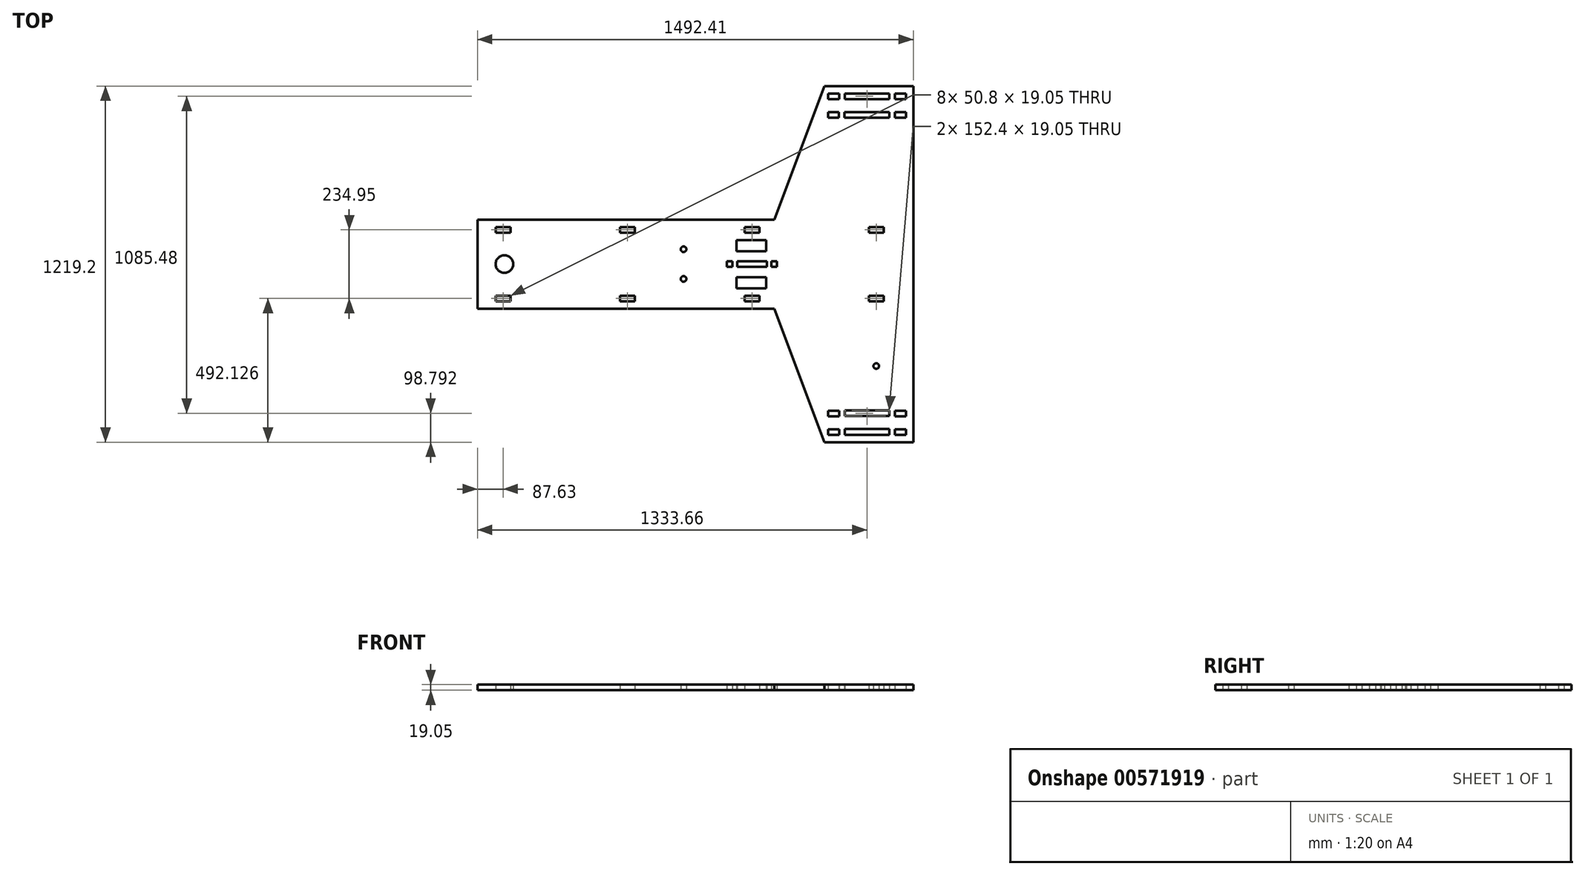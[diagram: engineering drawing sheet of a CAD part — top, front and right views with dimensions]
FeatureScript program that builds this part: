
annotation { "Feature Type Name" : "Feature", "Feature Type Description" : "" }
export const myFeature = defineFeature(function(context is Context, id is Id, definition is map)
    precondition{}
    {
        {
            var Q0;
            Q0=qCreatedBy(makeId("Top.planeOp"),FACE);
            var sketch = newSketch(context, id + "F0", { "sketchPlane" : qUnion([Q0])});
            skLineSegment(sketch, "E0.left", {"start": v(578, -643.36) * mm, "end": v(578, 575.84) * mm});
            skLineSegment(sketch, "E1.bottom", {"start": v(-914.4, 93.24) * mm, "end": v(101.6, 93.24) * mm});
            skLineSegment(sketch, "E1.top", {"start": v(-914.4, -186.16) * mm, "end": v(101.6, -186.16) * mm});
            skLineSegment(sketch, "E1.left", {"start": v(-914.4, 93.24) * mm, "end": v(-914.4, -186.16) * mm});
            skLineSegment(sketch, "E1.right", {"start": v(101.6, 93.24) * mm, "end": v(101.6, -186.16) * mm});
            skPoint(sketch, "E2.oppositeSnap0", {"position": v(-603.2, 271.04) * mm});
            skPoint(sketch, "E3.centerSnap0", {"position": v(-914.4, -46.46) * mm});
            skLineSegment(sketch, "E4.left", {"start": v(-914.4, -186.16) * mm, "end": v(-914.4, -167.1) * mm});
            skLineSegment(sketch, "E4.right", {"start": v(578, -186.16) * mm, "end": v(578, -167.1) * mm});
            skLineSegment(sketch, "E5.left", {"start": v(-914.4, 93.24) * mm, "end": v(-914.4, 74.2) * mm});
            skLineSegment(sketch, "E5.right", {"start": v(578, 93.24) * mm, "end": v(578, 74.2) * mm});
            skLineSegment(sketch, "E6", {"start": v(578, -643.36) * mm, "end": v(273.2, -643.36) * mm});
            skLineSegment(sketch, "E7", {"start": v(273.2, -643.36) * mm, "end": v(101.6, -186.16) * mm});
            skLineSegment(sketch, "E8", {"start": v(578, 575.84) * mm, "end": v(273.2, 575.84) * mm});
            skLineSegment(sketch, "E9.bottom", {"start": v(-852.17, -141.7) * mm, "end": v(-801.37, -141.7) * mm});
            skLineSegment(sketch, "E9.top", {"start": v(-852.17, -160.76) * mm, "end": v(-801.37, -160.76) * mm});
            skLineSegment(sketch, "E9.left", {"start": v(-852.17, -141.7) * mm, "end": v(-852.17, -160.76) * mm});
            skLineSegment(sketch, "E9.right", {"start": v(-801.37, -141.7) * mm, "end": v(-801.37, -160.76) * mm});
            skLineSegment(sketch, "E10", {"start": v(-852.17, -160.76) * mm, "end": v(101.6, -160.76) * mm});
            skLineSegment(sketch, "E11.bottom", {"start": v(-375.29, -160.76) * mm, "end": v(-426.09, -160.76) * mm});
            skLineSegment(sketch, "E11.top", {"start": v(-375.29, -141.7) * mm, "end": v(-426.09, -141.7) * mm});
            skLineSegment(sketch, "E11.left", {"start": v(-375.29, -160.76) * mm, "end": v(-375.29, -141.7) * mm});
            skLineSegment(sketch, "E11.right", {"start": v(-426.09, -160.76) * mm, "end": v(-426.09, -141.7) * mm});
            skLineSegment(sketch, "E12.bottom", {"start": v(0, -160.76) * mm, "end": v(50.8, -160.76) * mm});
            skLineSegment(sketch, "E12.top", {"start": v(0, -141.7) * mm, "end": v(50.8, -141.7) * mm});
            skLineSegment(sketch, "E12.left", {"start": v(0, -160.76) * mm, "end": v(0, -141.7) * mm});
            skLineSegment(sketch, "E12.right", {"start": v(50.8, -160.76) * mm, "end": v(50.8, -141.7) * mm});
            skLineSegment(sketch, "E13", {"start": v(101.6, -160.76) * mm, "end": v(578, -160.76) * mm});
            skLineSegment(sketch, "E14", {"start": v(101.6, 93.24) * mm, "end": v(578, 93.24) * mm});
            skLineSegment(sketch, "E15.bottom", {"start": v(426.09, -160.76) * mm, "end": v(476.89, -160.76) * mm});
            skLineSegment(sketch, "E15.top", {"start": v(426.09, -141.7) * mm, "end": v(476.89, -141.7) * mm});
            skLineSegment(sketch, "E15.left", {"start": v(426.09, -160.76) * mm, "end": v(426.09, -141.7) * mm});
            skLineSegment(sketch, "E15.right", {"start": v(476.89, -160.76) * mm, "end": v(476.89, -141.7) * mm});
            skLineSegment(sketch, "E16.bottom", {"start": v(101.6, 93.24) * mm, "end": v(-914.4, 93.24) * mm});
            skLineSegment(sketch, "E16.top", {"start": v(101.6, 118.64) * mm, "end": v(-914.4, 118.64) * mm});
            skLineSegment(sketch, "E16.left", {"start": v(101.6, 93.24) * mm, "end": v(101.6, 118.64) * mm});
            skLineSegment(sketch, "E16.right", {"start": v(-914.4, 93.24) * mm, "end": v(-914.4, 118.64) * mm});
            skLineSegment(sketch, "E17", {"start": v(101.6, 118.64) * mm, "end": v(273.2, 575.84) * mm});
            skLineSegment(sketch, "E18.bottom", {"start": v(-852.17, 93.24) * mm, "end": v(-801.37, 93.24) * mm});
            skLineSegment(sketch, "E18.top", {"start": v(-852.17, 74.2) * mm, "end": v(-801.37, 74.2) * mm});
            skLineSegment(sketch, "E18.left", {"start": v(-852.17, 93.24) * mm, "end": v(-852.17, 74.2) * mm});
            skLineSegment(sketch, "E18.right", {"start": v(-801.37, 93.24) * mm, "end": v(-801.37, 74.2) * mm});
            skLineSegment(sketch, "E19", {"start": v(-801.37, 93.24) * mm, "end": v(-426.08, 93.24) * mm});
            skLineSegment(sketch, "E20.bottom", {"start": v(-426.08, 93.24) * mm, "end": v(-375.28, 93.24) * mm});
            skLineSegment(sketch, "E20.top", {"start": v(-426.08, 74.2) * mm, "end": v(-375.28, 74.2) * mm});
            skLineSegment(sketch, "E20.left", {"start": v(-426.08, 93.24) * mm, "end": v(-426.08, 74.2) * mm});
            skLineSegment(sketch, "E20.right", {"start": v(-375.28, 93.24) * mm, "end": v(-375.28, 74.2) * mm});
            skLineSegment(sketch, "E21", {"start": v(-375.28, 93.24) * mm, "end": v(0, 93.24) * mm});
            skLineSegment(sketch, "E22.bottom", {"start": v(0, 93.24) * mm, "end": v(50.8, 93.24) * mm});
            skLineSegment(sketch, "E22.top", {"start": v(0, 74.2) * mm, "end": v(50.8, 74.2) * mm});
            skLineSegment(sketch, "E22.left", {"start": v(0, 93.24) * mm, "end": v(0, 74.2) * mm});
            skLineSegment(sketch, "E22.right", {"start": v(50.8, 93.24) * mm, "end": v(50.8, 74.2) * mm});
            skLineSegment(sketch, "E23", {"start": v(50.8, 93.24) * mm, "end": v(426.09, 93.24) * mm});
            skLineSegment(sketch, "E24.bottom", {"start": v(426.09, 93.24) * mm, "end": v(476.89, 93.24) * mm});
            skLineSegment(sketch, "E24.top", {"start": v(426.09, 74.2) * mm, "end": v(476.89, 74.2) * mm});
            skLineSegment(sketch, "E24.left", {"start": v(426.09, 93.24) * mm, "end": v(426.09, 74.2) * mm});
            skLineSegment(sketch, "E24.right", {"start": v(476.89, 93.24) * mm, "end": v(476.89, 74.2) * mm});
            skCircle(sketch, "E25", {"center": v(-822.05, -33.76) * mm, "radius": 30.12 * mm});
            skCircle(sketch, "E26", {"center": v(-208.68, 17.04) * mm, "radius": 9.53 * mm});
            skCircle(sketch, "E27", {"center": v(-208.68, -84.56) * mm, "radius": 9.53 * mm});
            skLineSegment(sketch, "E28.bottom", {"start": v(285.9, -598.9) * mm, "end": v(324, -598.9) * mm});
            skLineSegment(sketch, "E28.top", {"start": v(285.9, -617.96) * mm, "end": v(324, -617.96) * mm});
            skLineSegment(sketch, "E28.left", {"start": v(285.9, -598.9) * mm, "end": v(285.9, -617.96) * mm});
            skLineSegment(sketch, "E28.right", {"start": v(324, -598.9) * mm, "end": v(324, -617.96) * mm});
            skLineSegment(sketch, "E29.bottom", {"start": v(514.5, -617.96) * mm, "end": v(552.6, -617.96) * mm});
            skLineSegment(sketch, "E29.top", {"start": v(514.5, -598.9) * mm, "end": v(552.6, -598.9) * mm});
            skLineSegment(sketch, "E29.left", {"start": v(514.5, -617.96) * mm, "end": v(514.5, -598.9) * mm});
            skLineSegment(sketch, "E29.right", {"start": v(552.6, -617.96) * mm, "end": v(552.6, -598.9) * mm});
            skLineSegment(sketch, "E30.bottom", {"start": v(495.46, -598.54) * mm, "end": v(343.06, -598.54) * mm});
            skLineSegment(sketch, "E30.top", {"start": v(495.46, -617.96) * mm, "end": v(343.06, -617.96) * mm});
            skLineSegment(sketch, "E30.left", {"start": v(495.46, -598.54) * mm, "end": v(495.46, -617.96) * mm});
            skLineSegment(sketch, "E30.right", {"start": v(343.06, -598.54) * mm, "end": v(343.06, -617.96) * mm});
            skLineSegment(sketch, "E31.bottom", {"start": v(285.9, 550.44) * mm, "end": v(324, 550.44) * mm});
            skLineSegment(sketch, "E31.top", {"start": v(285.9, 531.4) * mm, "end": v(324, 531.4) * mm});
            skLineSegment(sketch, "E31.left", {"start": v(285.9, 550.44) * mm, "end": v(285.9, 531.4) * mm});
            skLineSegment(sketch, "E31.right", {"start": v(324, 550.44) * mm, "end": v(324, 531.4) * mm});
            skLineSegment(sketch, "E32.bottom", {"start": v(343.06, 550.44) * mm, "end": v(495.46, 550.44) * mm});
            skLineSegment(sketch, "E32.top", {"start": v(343.06, 531.4) * mm, "end": v(495.46, 531.4) * mm});
            skLineSegment(sketch, "E32.left", {"start": v(343.06, 550.44) * mm, "end": v(343.06, 531.4) * mm});
            skLineSegment(sketch, "E32.right", {"start": v(495.46, 550.44) * mm, "end": v(495.46, 531.4) * mm});
            skLineSegment(sketch, "E33.bottom", {"start": v(514.5, 550.44) * mm, "end": v(552.6, 550.44) * mm});
            skLineSegment(sketch, "E33.top", {"start": v(514.5, 531.4) * mm, "end": v(552.6, 531.4) * mm});
            skLineSegment(sketch, "E33.left", {"start": v(514.5, 550.44) * mm, "end": v(514.5, 531.4) * mm});
            skLineSegment(sketch, "E33.right", {"start": v(552.6, 550.44) * mm, "end": v(552.6, 531.4) * mm});
            skLineSegment(sketch, "E34.bottom", {"start": v(514.5, 486.94) * mm, "end": v(552.6, 486.94) * mm});
            skLineSegment(sketch, "E34.top", {"start": v(514.5, 467.9) * mm, "end": v(552.6, 467.9) * mm});
            skLineSegment(sketch, "E34.left", {"start": v(514.5, 486.94) * mm, "end": v(514.5, 467.9) * mm});
            skLineSegment(sketch, "E34.right", {"start": v(552.6, 486.94) * mm, "end": v(552.6, 467.9) * mm});
            skLineSegment(sketch, "E35.bottom", {"start": v(495.46, 486.94) * mm, "end": v(342.54, 486.94) * mm});
            skLineSegment(sketch, "E35.top", {"start": v(495.46, 468) * mm, "end": v(342.54, 468) * mm});
            skLineSegment(sketch, "E35.left", {"start": v(495.46, 486.94) * mm, "end": v(495.46, 468) * mm});
            skLineSegment(sketch, "E35.right", {"start": v(342.54, 486.94) * mm, "end": v(342.54, 468) * mm});
            skLineSegment(sketch, "E36.bottom", {"start": v(323.5, 486.94) * mm, "end": v(286.2, 486.94) * mm});
            skLineSegment(sketch, "E36.top", {"start": v(323.5, 467.9) * mm, "end": v(286.2, 467.9) * mm});
            skLineSegment(sketch, "E36.left", {"start": v(323.5, 486.94) * mm, "end": v(323.5, 467.9) * mm});
            skLineSegment(sketch, "E36.right", {"start": v(286.2, 486.94) * mm, "end": v(286.2, 467.9) * mm});
            skLineSegment(sketch, "E37.bottom", {"start": v(285.9, -535.4) * mm, "end": v(324, -535.4) * mm});
            skLineSegment(sketch, "E37.top", {"start": v(285.9, -554.46) * mm, "end": v(324, -554.46) * mm});
            skLineSegment(sketch, "E37.left", {"start": v(285.9, -535.4) * mm, "end": v(285.9, -554.46) * mm});
            skLineSegment(sketch, "E37.right", {"start": v(324, -535.4) * mm, "end": v(324, -554.46) * mm});
            skLineSegment(sketch, "E38.bottom", {"start": v(343.06, -535.04) * mm, "end": v(495.46, -535.04) * mm});
            skLineSegment(sketch, "E38.top", {"start": v(343.06, -554.1) * mm, "end": v(495.46, -554.1) * mm});
            skLineSegment(sketch, "E38.left", {"start": v(343.06, -535.04) * mm, "end": v(343.06, -554.1) * mm});
            skLineSegment(sketch, "E38.right", {"start": v(495.46, -535.04) * mm, "end": v(495.46, -554.1) * mm});
            skLineSegment(sketch, "E39.bottom", {"start": v(514.5, -554.46) * mm, "end": v(552.6, -554.46) * mm});
            skLineSegment(sketch, "E39.top", {"start": v(514.5, -535.4) * mm, "end": v(552.6, -535.4) * mm});
            skLineSegment(sketch, "E39.left", {"start": v(514.5, -554.46) * mm, "end": v(514.5, -535.4) * mm});
            skLineSegment(sketch, "E39.right", {"start": v(552.6, -554.46) * mm, "end": v(552.6, -535.4) * mm});
            skCircle(sketch, "E40", {"center": v(451, -382.64) * mm, "radius": 9.53 * mm});
            skLineSegment(sketch, "E41.bottom", {"start": v(-27.94, 48.8) * mm, "end": v(73.66, 48.8) * mm});
            skLineSegment(sketch, "E41.top", {"start": v(-27.94, 10.7) * mm, "end": v(73.66, 10.7) * mm});
            skLineSegment(sketch, "E41.left", {"start": v(-27.94, 48.8) * mm, "end": v(-27.94, 10.7) * mm});
            skLineSegment(sketch, "E41.right", {"start": v(73.66, 48.8) * mm, "end": v(73.66, 10.7) * mm});
            skLineSegment(sketch, "E42.bottom", {"start": v(-27.94, -78.2) * mm, "end": v(73.66, -78.2) * mm});
            skLineSegment(sketch, "E42.top", {"start": v(-27.94, -116.3) * mm, "end": v(73.66, -116.3) * mm});
            skLineSegment(sketch, "E42.left", {"start": v(-27.94, -78.2) * mm, "end": v(-27.94, -116.3) * mm});
            skLineSegment(sketch, "E42.right", {"start": v(73.66, -78.2) * mm, "end": v(73.66, -116.3) * mm});
            skLineSegment(sketch, "E43.left", {"start": v(24.75, -33.95) * mm, "end": v(24.75, -24.43) * mm});
            skLineSegment(sketch, "E44", {"start": v(24.75, 10.7) * mm, "end": v(24.75, -78.2) * mm});
            skLineSegment(sketch, "E45", {"start": v(24.75, -33.95) * mm, "end": v(-156.29, -33.95) * mm});
            skLineSegment(sketch, "E46.bottom", {"start": v(-60.32, -43.48) * mm, "end": v(-41.27, -43.48) * mm});
            skLineSegment(sketch, "E46.top", {"start": v(-60.32, -24.43) * mm, "end": v(-41.27, -24.43) * mm});
            skLineSegment(sketch, "E46.left", {"start": v(-60.32, -43.48) * mm, "end": v(-60.32, -24.43) * mm});
            skLineSegment(sketch, "E46.right", {"start": v(-41.27, -43.48) * mm, "end": v(-41.27, -24.43) * mm});
            skLineSegment(sketch, "E47.bottom", {"start": v(-25.4, -43.48) * mm, "end": v(76.2, -43.48) * mm});
            skLineSegment(sketch, "E47.top", {"start": v(-25.4, -24.43) * mm, "end": v(76.2, -24.43) * mm});
            skLineSegment(sketch, "E47.left", {"start": v(-25.4, -43.48) * mm, "end": v(-25.4, -24.43) * mm});
            skLineSegment(sketch, "E47.right", {"start": v(76.2, -43.48) * mm, "end": v(76.2, -24.43) * mm});
            skLineSegment(sketch, "E48.bottom", {"start": v(92.08, -43.48) * mm, "end": v(111.13, -43.48) * mm});
            skLineSegment(sketch, "E48.top", {"start": v(92.08, -24.43) * mm, "end": v(111.13, -24.43) * mm});
            skLineSegment(sketch, "E48.left", {"start": v(92.08, -43.48) * mm, "end": v(92.08, -24.43) * mm});
            skLineSegment(sketch, "E48.right", {"start": v(111.13, -43.48) * mm, "end": v(111.13, -24.43) * mm});
            skSolve(sketch);
        }
        {
            var Q0;
            Q0 = qSketchRegion(id + "F0", true);
            extrude(context, id + "F1", {"entities" : qUnion([Q0]), "depth" : 19.05 * mm, "offsetDistance" : 25.4 * mm});
        }
    });
